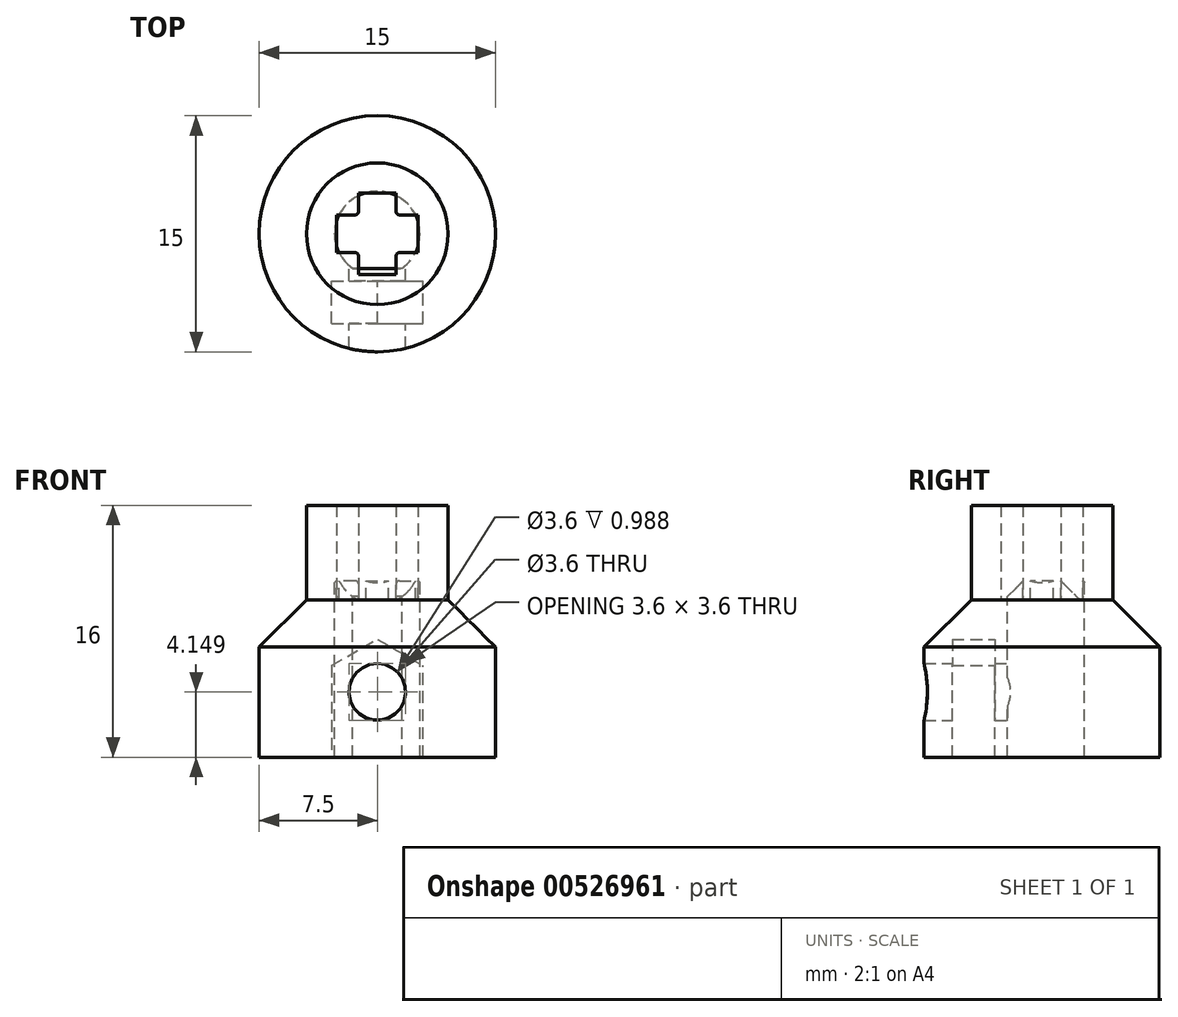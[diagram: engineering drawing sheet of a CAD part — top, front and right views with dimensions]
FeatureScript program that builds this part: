
annotation { "Feature Type Name" : "Feature", "Feature Type Description" : "" }
export const myFeature = defineFeature(function(context is Context, id is Id, definition is map)
    precondition{}
    {
        {
            var Q0;
            Q0=qCreatedBy(makeId("Top.planeOp"),FACE);
            var sketch = newSketch(context, id + "F0", { "sketchPlane" : qUnion([Q0])});
            skCircle(sketch, "E0", {"center": v(0, 0) * mm, "radius": 7.5 * mm});
            skCircle(sketch, "E1", {"center": v(0, 0) * mm, "radius": 2.7 * mm});
            skLineSegment(sketch, "E2", {"start": v(-1.57, -2.2) * mm, "end": v(1.57, -2.2) * mm});
            skSolve(sketch);
        }
        {
            var Q0;
            Q0=makeQuery(id+"F0.imprint","IMPRINT",FACE,{"disambiguationData":[TD([[makeQuery(id+"F0.imprint","IMPRINT",EDGE,{"derivedFrom":sQuery(id+"F0.wireOp",EDGE,"E0")}),1.0]])]});
            var Q1;
            {var subQ0=sQuery(id+"F0.wireOp",EDGE,"E2");Q1=makeQuery(id+"F0.imprint","IMPRINT",FACE,{"disambiguationData":[TD([[makeQuery(id+"F0.imprint","IMPRINT",EDGE,{"derivedFrom":subQ0}),-1.0]])]});}
            extrude(context, id + "F1", {"entities" : qUnion([Q0, Q1]), "oppositeDirection" : true, "depth" : 10 * mm, "offsetDistance" : 25 * mm});
        }
        {
            var Q0;
            Q0=qCreatedBy(makeId("Top.planeOp"),FACE);
            var sketch = newSketch(context, id + "F2", { "sketchPlane" : qUnion([Q0])});
            skCircle(sketch, "E3", {"center": v(0, 0) * mm, "radius": 4.5 * mm});
            skLineSegment(sketch, "E4.bottom", {"start": v(1.2, 2.6) * mm, "end": v(-1.2, 2.6) * mm});
            skLineSegment(sketch, "E4.top", {"start": v(1.2, -2.6) * mm, "end": v(-1.2, -2.6) * mm});
            skLineSegment(sketch, "E4.left", {"start": v(1.2, 2.6) * mm, "end": v(1.2, -2.6) * mm});
            skLineSegment(sketch, "E4.right", {"start": v(-1.2, 2.6) * mm, "end": v(-1.2, -2.6) * mm});
            skLineSegment(sketch, "E5.bottom", {"start": v(2.6, 1.2) * mm, "end": v(-2.6, 1.2) * mm});
            skLineSegment(sketch, "E5.top", {"start": v(2.6, -1.2) * mm, "end": v(-2.6, -1.2) * mm});
            skLineSegment(sketch, "E5.left", {"start": v(2.6, 1.2) * mm, "end": v(2.6, -1.2) * mm});
            skLineSegment(sketch, "E5.right", {"start": v(-2.6, 1.2) * mm, "end": v(-2.6, -1.2) * mm});
            skSolve(sketch);
        }
        {
            var Q0;
            Q0=makeQuery(id+"F2.imprint","IMPRINT",FACE,{"disambiguationData":[TD([[makeQuery(id+"F2.imprint","IMPRINT",EDGE,{"derivedFrom":sQuery(id+"F2.wireOp",EDGE,"E3")}),1.0]])]});
            extrude(context, id + "F3", {"entities" : qUnion([Q0]), "operationType" : NewBodyOperationType.ADD, "depth" : 6 * mm, "offsetDistance" : 25 * mm});
        }
        {
            var Q0;
            {var subQ0=sQuery(id+"F2.wireOp",EDGE,"E5.left");Q0=makeQuery(id+"F3.boolean.opBoolean","SPLIT",EDGE,{"disambiguationData":[topologyDisambiguationEdgeConnected([makeQuery(id+"F3.opExtrude","CAP_FACE",FACE,{"disambiguationData":[OSD([sQuery(id+"F2.wireOp",EDGE,"E3"),sQuery(id+"F2.wireOp",EDGE,"E4.bottom"),sQuery(id+"F2.wireOp",EDGE,"E4.top"),sQuery(id+"F2.wireOp",EDGE,"E4.left"),sQuery(id+"F2.wireOp",EDGE,"E4.right"),sQuery(id+"F2.wireOp",EDGE,"E5.bottom"),sQuery(id+"F2.wireOp",EDGE,"E5.top"),subQ0,sQuery(id+"F2.wireOp",EDGE,"E5.right")])],"isStart":true}),makeQuery(id+"F3.opExtrude","SWEPT_FACE",FACE,{"disambiguationData":[OSD([subQ0])]})])],"derivedFrom":makeQuery(id+"F3.opExtrude","CAP_EDGE",EDGE,{"disambiguationData":[OSD([subQ0])],"isStart":true})});}
            var Q1;
            {var subQ0=sQuery(id+"F2.wireOp",EDGE,"E4.bottom");Q1=makeQuery(id+"F3.boolean.opBoolean","SPLIT",EDGE,{"disambiguationData":[topologyDisambiguationEdgeConnected([makeQuery(id+"F3.opExtrude","CAP_FACE",FACE,{"disambiguationData":[OSD([sQuery(id+"F2.wireOp",EDGE,"E3"),subQ0,sQuery(id+"F2.wireOp",EDGE,"E4.top"),sQuery(id+"F2.wireOp",EDGE,"E4.left"),sQuery(id+"F2.wireOp",EDGE,"E4.right"),sQuery(id+"F2.wireOp",EDGE,"E5.bottom"),sQuery(id+"F2.wireOp",EDGE,"E5.top"),sQuery(id+"F2.wireOp",EDGE,"E5.left"),sQuery(id+"F2.wireOp",EDGE,"E5.right")])],"isStart":true}),makeQuery(id+"F3.opExtrude","SWEPT_FACE",FACE,{"disambiguationData":[OSD([subQ0])]})])],"derivedFrom":makeQuery(id+"F3.opExtrude","CAP_EDGE",EDGE,{"disambiguationData":[OSD([subQ0])],"isStart":true})});}
            var Q2;
            {var subQ0=sQuery(id+"F2.wireOp",EDGE,"E5.right");Q2=makeQuery(id+"F3.boolean.opBoolean","SPLIT",EDGE,{"disambiguationData":[topologyDisambiguationEdgeConnected([makeQuery(id+"F3.opExtrude","CAP_FACE",FACE,{"disambiguationData":[OSD([sQuery(id+"F2.wireOp",EDGE,"E3"),sQuery(id+"F2.wireOp",EDGE,"E4.bottom"),sQuery(id+"F2.wireOp",EDGE,"E4.top"),sQuery(id+"F2.wireOp",EDGE,"E4.left"),sQuery(id+"F2.wireOp",EDGE,"E4.right"),sQuery(id+"F2.wireOp",EDGE,"E5.bottom"),sQuery(id+"F2.wireOp",EDGE,"E5.top"),sQuery(id+"F2.wireOp",EDGE,"E5.left"),subQ0])],"isStart":true}),makeQuery(id+"F3.opExtrude","SWEPT_FACE",FACE,{"disambiguationData":[OSD([subQ0])]})])],"derivedFrom":makeQuery(id+"F3.opExtrude","CAP_EDGE",EDGE,{"disambiguationData":[OSD([subQ0])],"isStart":true})});}
            var Q3;
            {var subQ0=sQuery(id+"F2.wireOp",EDGE,"E5.right");var subQ1=sQuery(id+"F2.wireOp",EDGE,"E5.top");var subQ2=sQuery(id+"F2.wireOp",EDGE,"E4.right");var subQ3=makeQuery(id+"F2.imprint","IMPRINT",EDGE,{"disambiguationData":[TD([[makeQuery(id+"F2.imprint","INTERSECT",VERTEX,{"derivedFrom":[subQ1,subQ0]}),1.0]])],"derivedFrom":subQ1});Q3=makeQuery(id+"F3.boolean.opBoolean","SPLIT",EDGE,{"disambiguationData":[topologyDisambiguationEdgeConnected([makeQuery(id+"F3.opExtrude","CAP_FACE",FACE,{"disambiguationData":[OSD([sQuery(id+"F2.wireOp",EDGE,"E3"),sQuery(id+"F2.wireOp",EDGE,"E4.bottom"),sQuery(id+"F2.wireOp",EDGE,"E4.top"),sQuery(id+"F2.wireOp",EDGE,"E4.left"),subQ2,sQuery(id+"F2.wireOp",EDGE,"E5.bottom"),subQ1,sQuery(id+"F2.wireOp",EDGE,"E5.left"),subQ0])],"isStart":true})])],"derivedFrom":makeQuery(id+"F3.opExtrude","CAP_EDGE",EDGE,{"disambiguationData":[OSD([subQ1]),TDD([subQ3])],"isStart":true})});}
            var Q4;
            {var subQ0=sQuery(id+"F2.wireOp",EDGE,"E5.left");var subQ1=sQuery(id+"F2.wireOp",EDGE,"E5.top");var subQ2=sQuery(id+"F2.wireOp",EDGE,"E4.left");var subQ3=makeQuery(id+"F2.imprint","IMPRINT",EDGE,{"disambiguationData":[TD([[makeQuery(id+"F2.imprint","INTERSECT",VERTEX,{"derivedFrom":[subQ1,subQ0]}),-1.0]])],"derivedFrom":subQ1});Q4=makeQuery(id+"F3.boolean.opBoolean","SPLIT",EDGE,{"disambiguationData":[topologyDisambiguationEdgeConnected([makeQuery(id+"F3.opExtrude","CAP_FACE",FACE,{"disambiguationData":[OSD([sQuery(id+"F2.wireOp",EDGE,"E3"),sQuery(id+"F2.wireOp",EDGE,"E4.bottom"),sQuery(id+"F2.wireOp",EDGE,"E4.top"),subQ2,sQuery(id+"F2.wireOp",EDGE,"E4.right"),sQuery(id+"F2.wireOp",EDGE,"E5.bottom"),subQ1,subQ0,sQuery(id+"F2.wireOp",EDGE,"E5.right")])],"isStart":true})])],"derivedFrom":makeQuery(id+"F3.opExtrude","CAP_EDGE",EDGE,{"disambiguationData":[OSD([subQ1]),TDD([subQ3])],"isStart":true})});}
            var Q5;
            {var subQ0=sQuery(id+"F2.wireOp",EDGE,"E5.right");var subQ1=sQuery(id+"F2.wireOp",EDGE,"E5.bottom");var subQ2=sQuery(id+"F2.wireOp",EDGE,"E4.right");var subQ3=makeQuery(id+"F2.imprint","IMPRINT",EDGE,{"disambiguationData":[TD([[makeQuery(id+"F2.imprint","INTERSECT",VERTEX,{"derivedFrom":[subQ1,subQ0]}),1.0]])],"derivedFrom":subQ1});Q5=makeQuery(id+"F3.boolean.opBoolean","SPLIT",EDGE,{"disambiguationData":[topologyDisambiguationEdgeConnected([makeQuery(id+"F3.opExtrude","CAP_FACE",FACE,{"disambiguationData":[OSD([sQuery(id+"F2.wireOp",EDGE,"E3"),sQuery(id+"F2.wireOp",EDGE,"E4.bottom"),sQuery(id+"F2.wireOp",EDGE,"E4.top"),sQuery(id+"F2.wireOp",EDGE,"E4.left"),subQ2,subQ1,sQuery(id+"F2.wireOp",EDGE,"E5.top"),sQuery(id+"F2.wireOp",EDGE,"E5.left"),subQ0])],"isStart":true})])],"derivedFrom":makeQuery(id+"F3.opExtrude","CAP_EDGE",EDGE,{"disambiguationData":[OSD([subQ1]),TDD([subQ3])],"isStart":true})});}
            var Q6;
            {var subQ0=sQuery(id+"F2.wireOp",EDGE,"E5.left");var subQ1=sQuery(id+"F2.wireOp",EDGE,"E5.bottom");var subQ2=sQuery(id+"F2.wireOp",EDGE,"E4.left");var subQ3=makeQuery(id+"F2.imprint","IMPRINT",EDGE,{"disambiguationData":[TD([[makeQuery(id+"F2.imprint","INTERSECT",VERTEX,{"derivedFrom":[subQ1,subQ0]}),-1.0]])],"derivedFrom":subQ1});Q6=makeQuery(id+"F3.boolean.opBoolean","SPLIT",EDGE,{"disambiguationData":[topologyDisambiguationEdgeConnected([makeQuery(id+"F3.opExtrude","CAP_FACE",FACE,{"disambiguationData":[OSD([sQuery(id+"F2.wireOp",EDGE,"E3"),sQuery(id+"F2.wireOp",EDGE,"E4.bottom"),sQuery(id+"F2.wireOp",EDGE,"E4.top"),subQ2,sQuery(id+"F2.wireOp",EDGE,"E4.right"),subQ1,sQuery(id+"F2.wireOp",EDGE,"E5.top"),subQ0,sQuery(id+"F2.wireOp",EDGE,"E5.right")])],"isStart":true})])],"derivedFrom":makeQuery(id+"F3.opExtrude","CAP_EDGE",EDGE,{"disambiguationData":[OSD([subQ1]),TDD([subQ3])],"isStart":true})});}
            chamfer(context, id + "F4", {"entities" : qUnion([Q0, Q1, Q2, Q3, Q4, Q5, Q6]), "width" : 1.2 * mm, "tangentPropagation" : true});
        }
        {
            var Q0;
            Q0=makeQuery(id+"F3.opExtrude","SWEPT_EDGE",EDGE,{"disambiguationData":[OSD([sQuery(id+"F2.wireOp",EDGE,"E4.left"),sQuery(id+"F2.wireOp",EDGE,"E5.bottom")])]});
            var Q1;
            Q1=makeQuery(id+"F3.opExtrude","SWEPT_EDGE",EDGE,{"disambiguationData":[OSD([sQuery(id+"F2.wireOp",EDGE,"E4.left"),sQuery(id+"F2.wireOp",EDGE,"E5.top")])]});
            var Q2;
            Q2=makeQuery(id+"F3.opExtrude","SWEPT_EDGE",EDGE,{"disambiguationData":[OSD([sQuery(id+"F2.wireOp",EDGE,"E4.right"),sQuery(id+"F2.wireOp",EDGE,"E5.top")])]});
            var Q3;
            Q3=makeQuery(id+"F3.opExtrude","SWEPT_EDGE",EDGE,{"disambiguationData":[OSD([sQuery(id+"F2.wireOp",EDGE,"E4.right"),sQuery(id+"F2.wireOp",EDGE,"E5.bottom")])]});
            fillet(context, id + "F5", {"entities" : qUnion([Q0, Q1, Q2, Q3]), "radius" : 0.2 * mm, "tangentPropagation" : true, "allowEdgeOverflow" : false});
        }
        {
            var Q0;
            Q0=makeQuery(id+"F1.opExtrude","CAP_EDGE",EDGE,{"disambiguationData":[OSD([sQuery(id+"F0.wireOp",EDGE,"E0")])],"isStart":true});
            chamfer(context, id + "F6", {"entities" : qUnion([Q0]), "width" : (6 / 2) * mm, "tangentPropagation" : true});
        }
        {
            var Q0;
            Q0=qCreatedBy(makeId("Front.planeOp"),FACE);
            var sketch = newSketch(context, id + "F7", { "sketchPlane" : qUnion([Q0])});
            skCircle(sketch, "E6.cCircle", {"center": v(0, -5.85) * mm, "radius": 2.9 * mm, "construction": true});
            skLineSegment(sketch, "E6.0", {"start": v(2.9, -4.18) * mm, "end": v(2.9, -7.53) * mm});
            skLineSegment(sketch, "E6.1", {"start": v(2.9, -7.53) * mm, "end": v(0, -9.2) * mm});
            skLineSegment(sketch, "E6.2", {"start": v(0, -9.2) * mm, "end": v(-2.9, -7.53) * mm});
            skLineSegment(sketch, "E6.3", {"start": v(-2.9, -7.53) * mm, "end": v(-2.9, -4.18) * mm});
            skLineSegment(sketch, "E6.4", {"start": v(-2.9, -4.18) * mm, "end": v(0, -2.5) * mm});
            skLineSegment(sketch, "E6.5", {"start": v(0, -2.5) * mm, "end": v(2.9, -4.18) * mm});
            skPoint(sketch, "E6.0.midPoint", {"position": v(2.9, -5.85) * mm});
            skLineSegment(sketch, "E7", {"start": v(-2.9, -7.53) * mm, "end": v(-2.9, -10) * mm});
            skLineSegment(sketch, "E8", {"start": v(-2.9, -10) * mm, "end": v(2.9, -10) * mm});
            skLineSegment(sketch, "E9", {"start": v(2.9, -10) * mm, "end": v(2.9, -7.53) * mm});
            skCircle(sketch, "E10", {"center": v(0, -5.85) * mm, "radius": 1.8 * mm});
            skSolve(sketch);
        }
        {
            var Q0;
            Q0=makeQuery(id+"F7.imprint","IMPRINT",FACE,{"disambiguationData":[TD([[makeQuery(id+"F7.imprint","IMPRINT",EDGE,{"derivedFrom":sQuery(id+"F7.wireOp",EDGE,"E6.1")}),1.0]])]});
            var Q1;
            Q1=makeQuery(id+"F7.imprint","IMPRINT",FACE,{"disambiguationData":[TD([[makeQuery(id+"F7.imprint","IMPRINT",EDGE,{"derivedFrom":sQuery(id+"F7.wireOp",EDGE,"E6.0")}),-1.0]])]});
            extrude(context, id + "F8", {"entities" : qUnion([Q0, Q1]), "operationType" : NewBodyOperationType.REMOVE, "depth" : (2.2 + 0.8 + 2.7) * mm, "offsetDistance" : 25 * mm, "hasSecondDirection" : true, "secondDirectionOppositeDirection" : false, "secondDirectionDepth" : (2.2 + 0.8) * mm});
        }
        {
            var Q0;
            Q0=makeQuery(id+"F7.imprint","IMPRINT",FACE,{"disambiguationData":[TD([[makeQuery(id+"F7.imprint","IMPRINT",EDGE,{"derivedFrom":sQuery(id+"F7.wireOp",EDGE,"E10")}),1.0]])]});
            var Q1;
            Q1=makeQuery(id+"F1.opExtrude","SWEPT_FACE",FACE,{"disambiguationData":[OSD([sQuery(id+"F0.wireOp",EDGE,"E0")])]});
            extrude(context, id + "F9", {"entities" : qUnion([Q0]), "operationType" : NewBodyOperationType.REMOVE, "endBound" : BoundingType.UP_TO_SURFACE, "depth" : 25 * mm, "endBoundEntityFace" : qUnion([Q1]), "offsetDistance" : 25 * mm});
        }
    });
